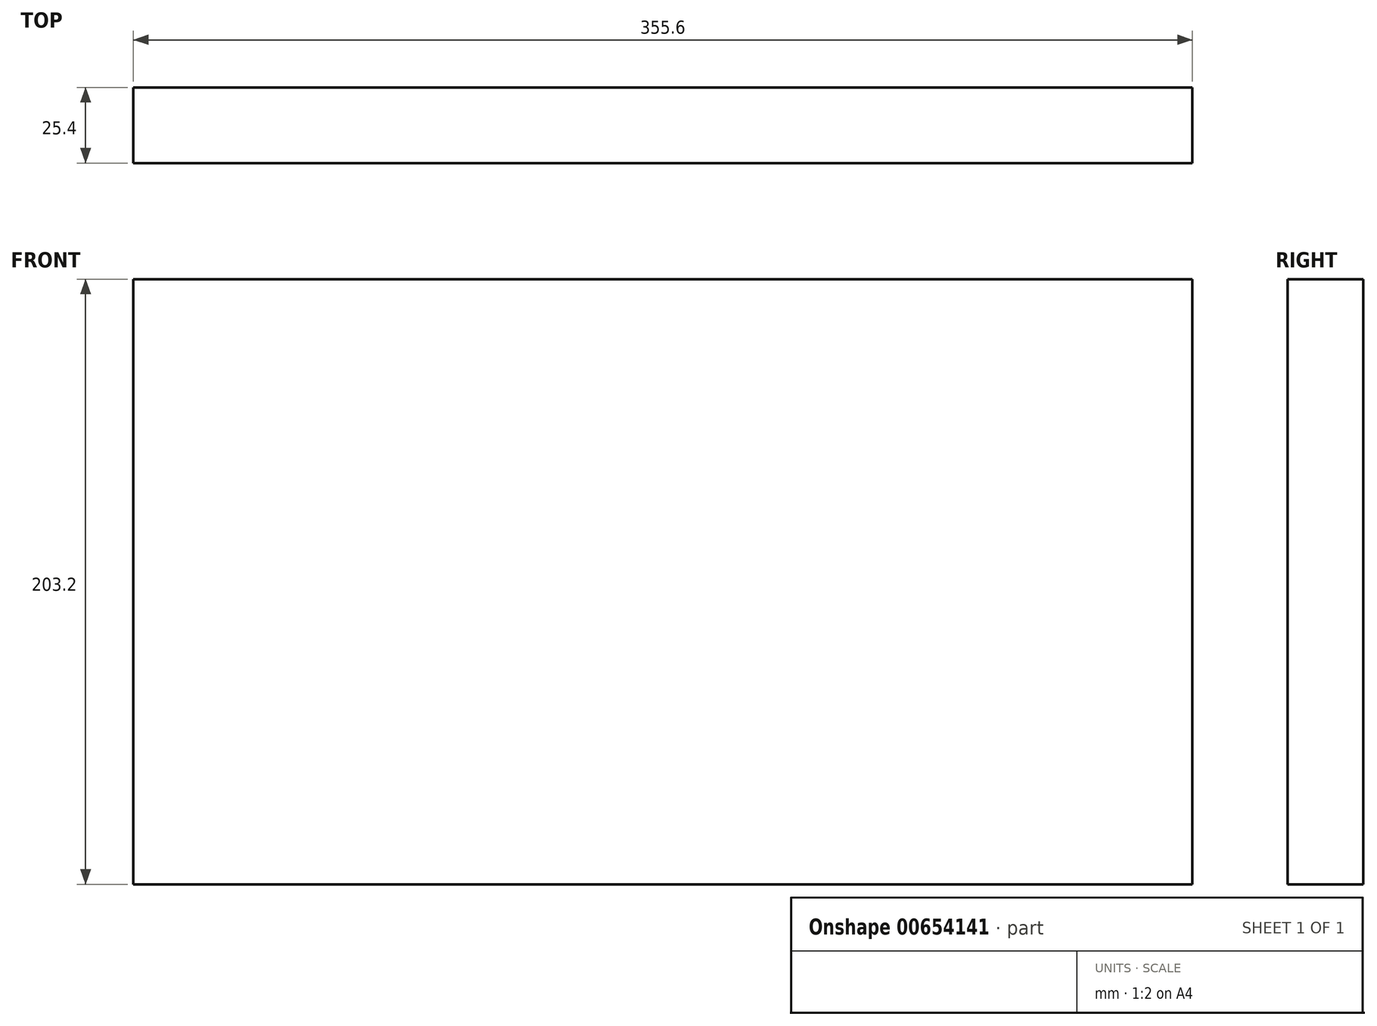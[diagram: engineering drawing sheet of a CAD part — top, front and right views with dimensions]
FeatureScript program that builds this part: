
annotation { "Feature Type Name" : "Feature", "Feature Type Description" : "" }
export const myFeature = defineFeature(function(context is Context, id is Id, definition is map)
    precondition{}
    {
        {
            var Q0;
            Q0=qCreatedBy(makeId("Front.planeOp"),FACE);
            var sketch = newSketch(context, id + "F0", { "sketchPlane" : qUnion([Q0])});
            skLineSegment(sketch, "E0.bottom", {"start": v(-237.26, 93.39) * mm, "end": v(118.34, 93.39) * mm});
            skLineSegment(sketch, "E0.top", {"start": v(-237.26, -109.81) * mm, "end": v(118.34, -109.81) * mm});
            skLineSegment(sketch, "E0.left", {"start": v(-237.26, 93.39) * mm, "end": v(-237.26, -109.81) * mm});
            skLineSegment(sketch, "E0.right", {"start": v(118.34, 93.39) * mm, "end": v(118.34, -109.81) * mm});
            skSolve(sketch);
        }
        {
            var Q0;
            Q0=makeQuery(id+"F0.imprint","IMPRINT",FACE,{"disambiguationData":[TD([[makeQuery(id+"F0.imprint","IMPRINT",EDGE,{"derivedFrom":sQuery(id+"F0.wireOp",EDGE,"E0.bottom")}),-1.0]])]});
            extrude(context, id + "F1", {"entities" : qUnion([Q0]), "depth" : 25.4 * mm, "offsetDistance" : 25.4 * mm});
        }
    });
